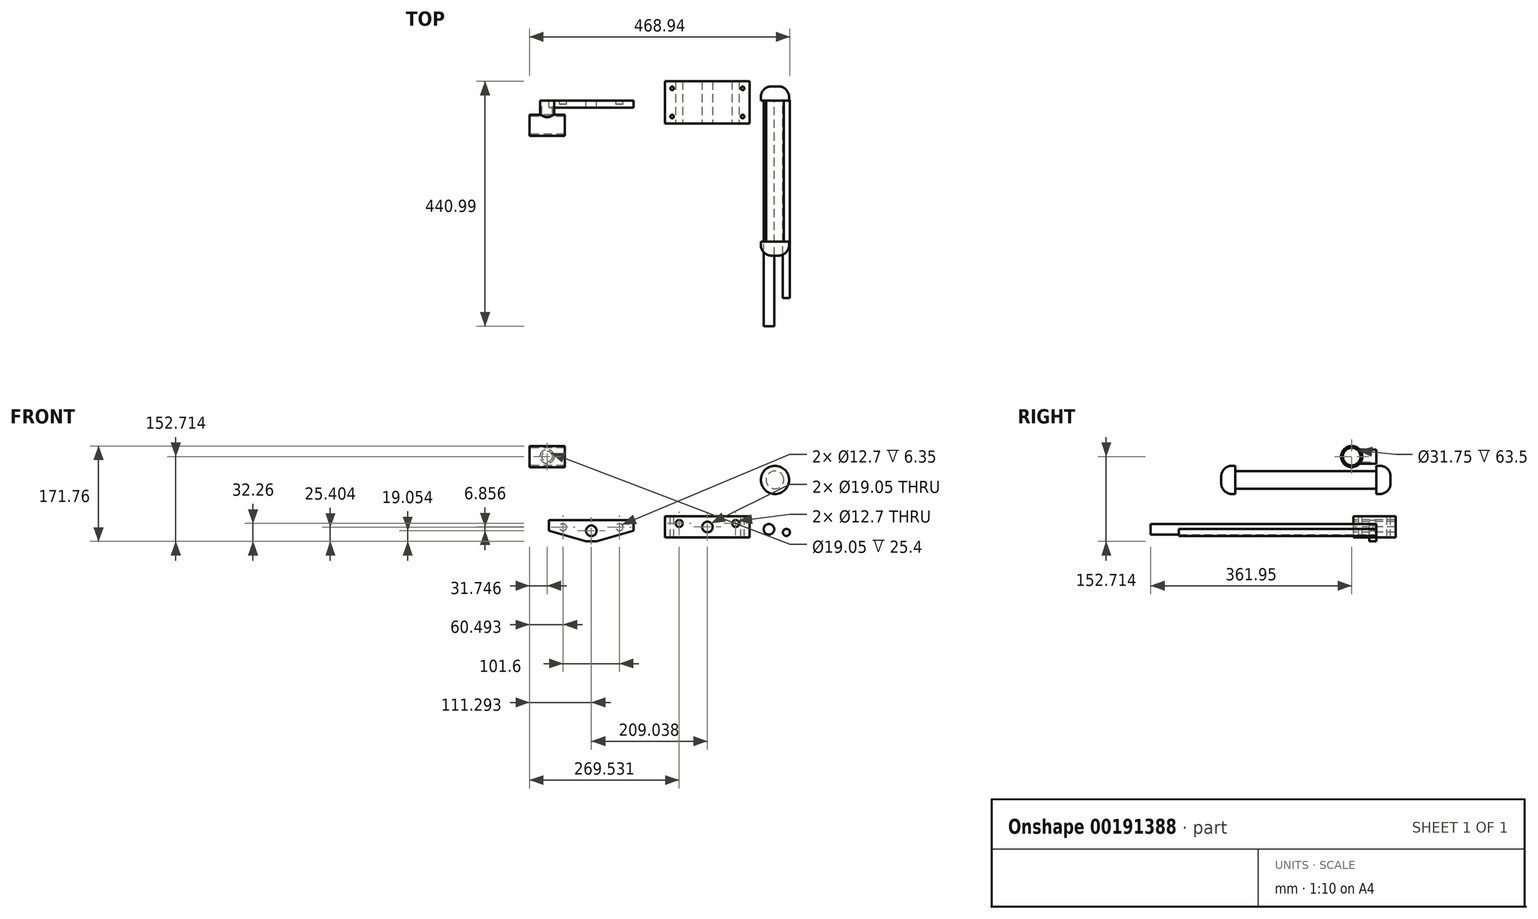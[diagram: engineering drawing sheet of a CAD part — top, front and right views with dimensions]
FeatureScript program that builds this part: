
annotation { "Feature Type Name" : "Feature", "Feature Type Description" : "" }
export const myFeature = defineFeature(function(context is Context, id is Id, definition is map)
    precondition{}
    {
        {
            var Q0;
            Q0=qCreatedBy(makeId("Top.planeOp"),FACE);
            var sketch = newSketch(context, id + "F0", { "sketchPlane" : qUnion([Q0])});
            skLineSegment(sketch, "E0.bottom", {"start": v(-58.83, 34.6) * mm, "end": v(93.57, 34.6) * mm});
            skLineSegment(sketch, "E0.top", {"start": v(-58.83, -41.6) * mm, "end": v(93.57, -41.6) * mm});
            skLineSegment(sketch, "E0.left", {"start": v(-58.83, 34.6) * mm, "end": v(-58.83, -41.6) * mm});
            skLineSegment(sketch, "E0.right", {"start": v(93.57, 34.6) * mm, "end": v(93.57, -41.6) * mm});
            skSolve(sketch);
        }
        {
            var Q0;
            Q0=makeQuery(id+"F0.imprint","IMPRINT",FACE,{"disambiguationData":[TD([[makeQuery(id+"F0.imprint","IMPRINT",EDGE,{"derivedFrom":sQuery(id+"F0.wireOp",EDGE,"E0.bottom")}),-1.0]])]});
            extrude(context, id + "F1", {"entities" : qUnion([Q0]), "depth" : 38.1 * mm});
        }
        {
            var Q0;
            Q0=makeQuery(id+"F1.opExtrude","SWEPT_FACE",FACE,{"disambiguationData":[OSD([sQuery(id+"F0.wireOp",EDGE,"E0.top")])]});
            var sketch = newSketch(context, id + "F2", { "sketchPlane" : qUnion([Q0])});
            skCircle(sketch, "E1", {"center": v(-33.43, 25.4) * mm, "radius": 6.35 * mm});
            skCircle(sketch, "E2", {"center": v(68.17, 25.4) * mm, "radius": 6.35 * mm});
            skCircle(sketch, "E3", {"center": v(17.37, 19.05) * mm, "radius": 9.53 * mm});
            skLineSegment(sketch, "E4", {"start": v(17.37, 38.1) * mm, "end": v(17.37, 0) * mm, "construction": true});
            skSolve(sketch);
        }
        {
            var Q0;
            Q0 = qSketchRegion(id + "F2", true);
            extrude(context, id + "F3", {"entities" : qUnion([Q0]), "operationType" : NewBodyOperationType.REMOVE, "endBound" : BoundingType.UP_TO_NEXT, "oppositeDirection" : true, "depth" : 25.4 * mm});
        }
        {
            var Q0;
            Q0=makeQuery(id+"F1.opExtrude","CAP_FACE",FACE,{"disambiguationData":[OSD([sQuery(id+"F0.wireOp",EDGE,"E0.bottom"),sQuery(id+"F0.wireOp",EDGE,"E0.top"),sQuery(id+"F0.wireOp",EDGE,"E0.left"),sQuery(id+"F0.wireOp",EDGE,"E0.right")])],"isStart":false});
            var sketch = newSketch(context, id + "F4", { "sketchPlane" : qUnion([Q0])});
            skCircle(sketch, "E5", {"center": v(-46.13, 21.9) * mm, "radius": 3.18 * mm});
            skCircle(sketch, "E6", {"center": v(-46.13, -28.9) * mm, "radius": 3.18 * mm});
            skCircle(sketch, "E7", {"center": v(80.87, 21.9) * mm, "radius": 3.18 * mm});
            skCircle(sketch, "E8", {"center": v(80.87, -28.9) * mm, "radius": 3.18 * mm});
            skSolve(sketch);
        }
        {
            var Q0;
            Q0 = qSketchRegion(id + "F4", true);
            extrude(context, id + "F5", {"entities" : qUnion([Q0]), "operationType" : NewBodyOperationType.REMOVE, "endBound" : BoundingType.UP_TO_NEXT, "oppositeDirection" : true, "depth" : 25.4 * mm});
        }
        {
            var Q0;
            Q0=qCreatedBy(makeId("Front.planeOp"),FACE);
            var sketch = newSketch(context, id + "F6", { "sketchPlane" : qUnion([Q0])});
            skCircle(sketch, "E9", {"center": v(159.63, 9.27) * mm, "radius": 6.35 * mm});
            skSolve(sketch);
        }
        {
            var Q0;
            Q0 = qSketchRegion(id + "F6", true);
            extrude(context, id + "F7", {"entities" : qUnion([Q0]), "depth" : 355.6 * mm});
        }
        {
            var Q0;
            Q0=qCreatedBy(makeId("Front.planeOp"),FACE);
            var sketch = newSketch(context, id + "F8", { "sketchPlane" : qUnion([Q0])});
            skCircle(sketch, "E10", {"center": v(128.23, 14.83) * mm, "radius": 9.53 * mm});
            skSolve(sketch);
        }
        {
            var Q0;
            Q0 = qSketchRegion(id + "F8", true);
            extrude(context, id + "F9", {"entities" : qUnion([Q0]), "depth" : 406.4 * mm});
        }
        {
            var Q0;
            Q0=qCreatedBy(makeId("Front.planeOp"),FACE);
            var sketch = newSketch(context, id + "F10", { "sketchPlane" : qUnion([Q0])});
            skLineSegment(sketch, "E11", {"start": v(-115.47, 31.24) * mm, "end": v(-267.87, 31.24) * mm});
            skLineSegment(sketch, "E12", {"start": v(-267.87, 31.24) * mm, "end": v(-267.87, 12.2) * mm});
            skLineSegment(sketch, "E13", {"start": v(-267.87, 12.2) * mm, "end": v(-201.2, -6.86) * mm});
            skLineSegment(sketch, "E14", {"start": v(-201.2, -6.86) * mm, "end": v(-182.14, -6.86) * mm});
            skLineSegment(sketch, "E15", {"start": v(-182.14, -6.86) * mm, "end": v(-115.47, 12.2) * mm});
            skLineSegment(sketch, "E16", {"start": v(-115.47, 12.2) * mm, "end": v(-115.47, 31.24) * mm});
            skLineSegment(sketch, "E17", {"start": v(-191.67, -6.86) * mm, "end": v(-191.67, 31.24) * mm, "construction": true});
            skSolve(sketch);
        }
        {
            var Q0;
            Q0=makeQuery(id+"F10.imprint","IMPRINT",FACE,{"disambiguationData":[TD([[makeQuery(id+"F10.imprint","IMPRINT",EDGE,{"derivedFrom":sQuery(id+"F10.wireOp",EDGE,"E11")}),1.0]])]});
            extrude(context, id + "F11", {"entities" : qUnion([Q0]), "depth" : 12.7 * mm});
        }
        {
            var Q0;
            Q0=makeQuery(id+"F11.opExtrude","CAP_FACE",FACE,{"disambiguationData":[OSD([sQuery(id+"F10.wireOp",EDGE,"E11"),sQuery(id+"F10.wireOp",EDGE,"E12"),sQuery(id+"F10.wireOp",EDGE,"E13"),sQuery(id+"F10.wireOp",EDGE,"E14"),sQuery(id+"F10.wireOp",EDGE,"E15"),sQuery(id+"F10.wireOp",EDGE,"E16")])],"isStart":true});
            var sketch = newSketch(context, id + "F12", { "sketchPlane" : qUnion([Q0])});
            skCircle(sketch, "E18", {"center": v(242.47, 18.54) * mm, "radius": 6.35 * mm});
            skCircle(sketch, "E19", {"center": v(140.87, 18.54) * mm, "radius": 6.35 * mm});
            skLineSegment(sketch, "E20", {"start": v(191.67, 31.24) * mm, "end": v(191.67, -6.86) * mm, "construction": true});
            skSolve(sketch);
        }
        {
            var Q0;
            Q0 = qSketchRegion(id + "F12", true);
            extrude(context, id + "F13", {"entities" : qUnion([Q0]), "operationType" : NewBodyOperationType.REMOVE, "oppositeDirection" : true, "depth" : 6.35 * mm});
        }
        {
            var Q0;
            Q0=makeQuery(id+"F11.opExtrude","CAP_FACE",FACE,{"disambiguationData":[OSD([sQuery(id+"F10.wireOp",EDGE,"E11"),sQuery(id+"F10.wireOp",EDGE,"E12"),sQuery(id+"F10.wireOp",EDGE,"E13"),sQuery(id+"F10.wireOp",EDGE,"E14"),sQuery(id+"F10.wireOp",EDGE,"E15"),sQuery(id+"F10.wireOp",EDGE,"E16")])],"isStart":true});
            var sketch = newSketch(context, id + "F14", { "sketchPlane" : qUnion([Q0])});
            skCircle(sketch, "E21", {"center": v(191.67, 12.2) * mm, "radius": 9.53 * mm});
            skPoint(sketch, "E21.centerSnap0", {"position": v(191.67, -6.86) * mm});
            skSolve(sketch);
        }
        {
            var Q0;
            Q0=makeQuery(id+"F14.imprint","IMPRINT",FACE,{"disambiguationData":[TD([[makeQuery(id+"F14.imprint","IMPRINT",EDGE,{"derivedFrom":sQuery(id+"F14.wireOp",EDGE,"E21")}),1.0]])]});
            var Q1;
            Q1=sQuery(id+"F14.wireOp",EDGE,"E21");
            extrude(context, id + "F15", {"entities" : qUnion([Q0]), "operationType" : NewBodyOperationType.REMOVE, "surfaceEntities" : qUnion([Q1]), "oppositeDirection" : true, "depth" : 25.4 * mm});
        }
        {
            var Q0;
            Q0=qCreatedBy(makeId("Front.planeOp"),FACE);
            var sketch = newSketch(context, id + "F16", { "sketchPlane" : qUnion([Q0])});
            skLineSegment(sketch, "E22.bottom", {"start": v(-283.91, 158.55) * mm, "end": v(-258.51, 158.55) * mm});
            skLineSegment(sketch, "E22.top", {"start": v(-283.91, 133.15) * mm, "end": v(-258.51, 133.15) * mm});
            skLineSegment(sketch, "E22.left", {"start": v(-283.91, 158.55) * mm, "end": v(-283.91, 133.15) * mm});
            skLineSegment(sketch, "E22.right", {"start": v(-258.51, 158.55) * mm, "end": v(-258.51, 133.15) * mm});
            skSolve(sketch);
        }
        {
            var Q0;
            Q0=makeQuery(id+"F16.imprint","IMPRINT",FACE,{"disambiguationData":[TD([[makeQuery(id+"F16.imprint","IMPRINT",EDGE,{"derivedFrom":sQuery(id+"F16.wireOp",EDGE,"E22.bottom")}),-1.0]])]});
            extrude(context, id + "F17", {"entities" : qUnion([Q0]), "depth" : 25.4 * mm});
        }
        {
            var Q0;
            Q0=makeQuery(id+"F17.opExtrude","SWEPT_FACE",FACE,{"disambiguationData":[OSD([sQuery(id+"F16.wireOp",EDGE,"E22.bottom")])]});
            cPlane(context, id + "F18", {"entities" : qUnion([Q0]), "cplaneType" : CPlaneType.OFFSET, "offset" : 12.7 * mm, "oppositeDirection" : true, "width" : 152.4 * mm, "height" : 152.4 * mm});
        }
        {
            var Q0;
            Q0=qCreatedBy(id+"F18.planeOp",FACE);
            var sketch = newSketch(context, id + "F19", { "sketchPlane" : qUnion([Q0])});
            skLineSegment(sketch, "E23.bottom", {"start": v(-302.96, -63.5) * mm, "end": v(-239.46, -63.5) * mm});
            skLineSegment(sketch, "E23.top", {"start": v(-302.96, -25.4) * mm, "end": v(-239.46, -25.4) * mm});
            skLineSegment(sketch, "E23.left", {"start": v(-302.96, -63.5) * mm, "end": v(-302.96, -25.4) * mm});
            skLineSegment(sketch, "E23.right", {"start": v(-239.46, -63.5) * mm, "end": v(-239.46, -25.4) * mm});
            skPoint(sketch, "E24", {"position": v(-271.21, -25.4) * mm});
            skSolve(sketch);
        }
        {
            var Q0;
            Q0 = qSketchRegion(id + "F19", true);
            extrude(context, id + "F20", {"entities" : qUnion([Q0]), "operationType" : NewBodyOperationType.ADD, "endBound" : BoundingType.SYMMETRIC, "depth" : 38.1 * mm});
        }
        {
            var Q0;
            Q0=makeQuery(id+"F17.opExtrude","SWEPT_EDGE",EDGE,{"disambiguationData":[OSD([sQuery(id+"F16.wireOp",EDGE,"E22.bottom"),sQuery(id+"F16.wireOp",EDGE,"E22.left")])]});
            var Q1;
            Q1=makeQuery(id+"F17.opExtrude","SWEPT_EDGE",EDGE,{"disambiguationData":[OSD([sQuery(id+"F16.wireOp",EDGE,"E22.bottom"),sQuery(id+"F16.wireOp",EDGE,"E22.right")])]});
            var Q2;
            Q2=makeQuery(id+"F17.opExtrude","SWEPT_EDGE",EDGE,{"disambiguationData":[OSD([sQuery(id+"F16.wireOp",EDGE,"E22.top"),sQuery(id+"F16.wireOp",EDGE,"E22.left")])]});
            var Q3;
            Q3=makeQuery(id+"F17.opExtrude","SWEPT_EDGE",EDGE,{"disambiguationData":[OSD([sQuery(id+"F16.wireOp",EDGE,"E22.top"),sQuery(id+"F16.wireOp",EDGE,"E22.right")])]});
            fillet(context, id + "F21", {"entities" : qUnion([Q0, Q1, Q2, Q3]), "radius" : 12.7 * mm, "tangentPropagation" : true, "allowEdgeOverflow" : false});
        }
        {
            var Q0;
            Q0=makeQuery(id+"F20.opExtrude","CAP_EDGE",EDGE,{"disambiguationData":[OSD([sQuery(id+"F19.wireOp",EDGE,"E23.top")])],"isStart":false});
            var Q1;
            Q1=makeQuery(id+"F20.opExtrude","CAP_EDGE",EDGE,{"disambiguationData":[OSD([sQuery(id+"F19.wireOp",EDGE,"E23.top")])],"isStart":true});
            var Q2;
            Q2=makeQuery(id+"F20.opExtrude","CAP_EDGE",EDGE,{"disambiguationData":[OSD([sQuery(id+"F19.wireOp",EDGE,"E23.bottom")])],"isStart":false});
            var Q3;
            Q3=makeQuery(id+"F20.opExtrude","CAP_EDGE",EDGE,{"disambiguationData":[OSD([sQuery(id+"F19.wireOp",EDGE,"E23.bottom")])],"isStart":true});
            fillet(context, id + "F22", {"entities" : qUnion([Q0, Q1, Q2, Q3]), "radius" : 19.05 * mm, "tangentPropagation" : true, "allowEdgeOverflow" : false});
        }
        {
            var Q0;
            Q0=makeQuery(id+"F20.opExtrude","SWEPT_FACE",FACE,{"disambiguationData":[OSD([sQuery(id+"F19.wireOp",EDGE,"E23.left")])]});
            var sketch = newSketch(context, id + "F23", { "sketchPlane" : qUnion([Q0])});
            skCircle(sketch, "E25", {"center": v(44.45, 145.85) * mm, "radius": 15.88 * mm});
            skSolve(sketch);
        }
        {
            var Q0;
            Q0=makeQuery(id+"F23.imprint","IMPRINT",FACE,{"disambiguationData":[TD([[makeQuery(id+"F23.imprint","IMPRINT",EDGE,{"derivedFrom":sQuery(id+"F23.wireOp",EDGE,"E25")}),1.0]])]});
            var Q1;
            Q1=sQuery(id+"F23.wireOp",EDGE,"E25");
            extrude(context, id + "F24", {"entities" : qUnion([Q0]), "operationType" : NewBodyOperationType.REMOVE, "surfaceEntities" : qUnion([Q1]), "endBound" : BoundingType.UP_TO_NEXT, "oppositeDirection" : true, "depth" : 25.4 * mm});
        }
        {
            var Q0;
            Q0=makeQuery(id+"F17.opExtrude","CAP_FACE",FACE,{"disambiguationData":[OSD([sQuery(id+"F16.wireOp",EDGE,"E22.bottom"),sQuery(id+"F16.wireOp",EDGE,"E22.top"),sQuery(id+"F16.wireOp",EDGE,"E22.left"),sQuery(id+"F16.wireOp",EDGE,"E22.right")])],"isStart":true});
            var sketch = newSketch(context, id + "F25", { "sketchPlane" : qUnion([Q0])});
            skCircle(sketch, "E26", {"center": v(271.21, 145.85) * mm, "radius": 9.53 * mm});
            skSolve(sketch);
        }
        {
            var Q0;
            Q0 = qSketchRegion(id + "F25", true);
            extrude(context, id + "F26", {"entities" : qUnion([Q0]), "operationType" : NewBodyOperationType.REMOVE, "oppositeDirection" : true, "depth" : 25.4 * mm});
        }
        {
            var Q0;
            Q0=qCreatedBy(makeId("Front.planeOp"),FACE);
            var sketch = newSketch(context, id + "F27", { "sketchPlane" : qUnion([Q0])});
            skCircle(sketch, "E27", {"center": v(138.98, 103.89) * mm, "radius": 15.88 * mm});
            skSolve(sketch);
        }
        {
            var Q0;
            Q0 = qSketchRegion(id + "F27", true);
            extrude(context, id + "F28", {"entities" : qUnion([Q0]), "depth" : 254 * mm});
        }
        {
            var Q0;
            Q0=makeQuery(id+"F28.opExtrude","CAP_FACE",FACE,{"disambiguationData":[OSD([sQuery(id+"F27.wireOp",EDGE,"E27")])],"isStart":false});
            var sketch = newSketch(context, id + "F29", { "sketchPlane" : qUnion([Q0])});
            skCircle(sketch, "E28", {"center": v(138.98, 103.89) * mm, "radius": 25.4 * mm});
            skSolve(sketch);
        }
        {
            var Q0;
            Q0 = qSketchRegion(id + "F29", true);
            extrude(context, id + "F30", {"entities" : qUnion([Q0]), "operationType" : NewBodyOperationType.ADD, "depth" : 25.4 * mm});
        }
        {
            var Q0;
            Q0=makeQuery(id+"F28.opExtrude","CAP_FACE",FACE,{"disambiguationData":[OSD([sQuery(id+"F27.wireOp",EDGE,"E27")])],"isStart":true});
            var sketch = newSketch(context, id + "F31", { "sketchPlane" : qUnion([Q0])});
            skCircle(sketch, "E29", {"center": v(-138.98, 103.89) * mm, "radius": 25.4 * mm});
            skSolve(sketch);
        }
        {
            var Q0;
            Q0 = qSketchRegion(id + "F31", true);
            extrude(context, id + "F32", {"entities" : qUnion([Q0]), "operationType" : NewBodyOperationType.ADD, "depth" : 25.4 * mm});
        }
        {
            var Q0;
            Q0=makeQuery(id+"F30.opExtrude","CAP_EDGE",EDGE,{"disambiguationData":[OSD([sQuery(id+"F29.wireOp",EDGE,"E28")])],"isStart":false});
            var Q1;
            Q1=makeQuery(id+"F32.opExtrude","CAP_EDGE",EDGE,{"disambiguationData":[OSD([sQuery(id+"F31.wireOp",EDGE,"E29")])],"isStart":false});
            fillet(context, id + "F33", {"entities" : qUnion([Q0, Q1]), "radius" : 19.05 * mm, "tangentPropagation" : true, "allowEdgeOverflow" : false});
        }
    });
